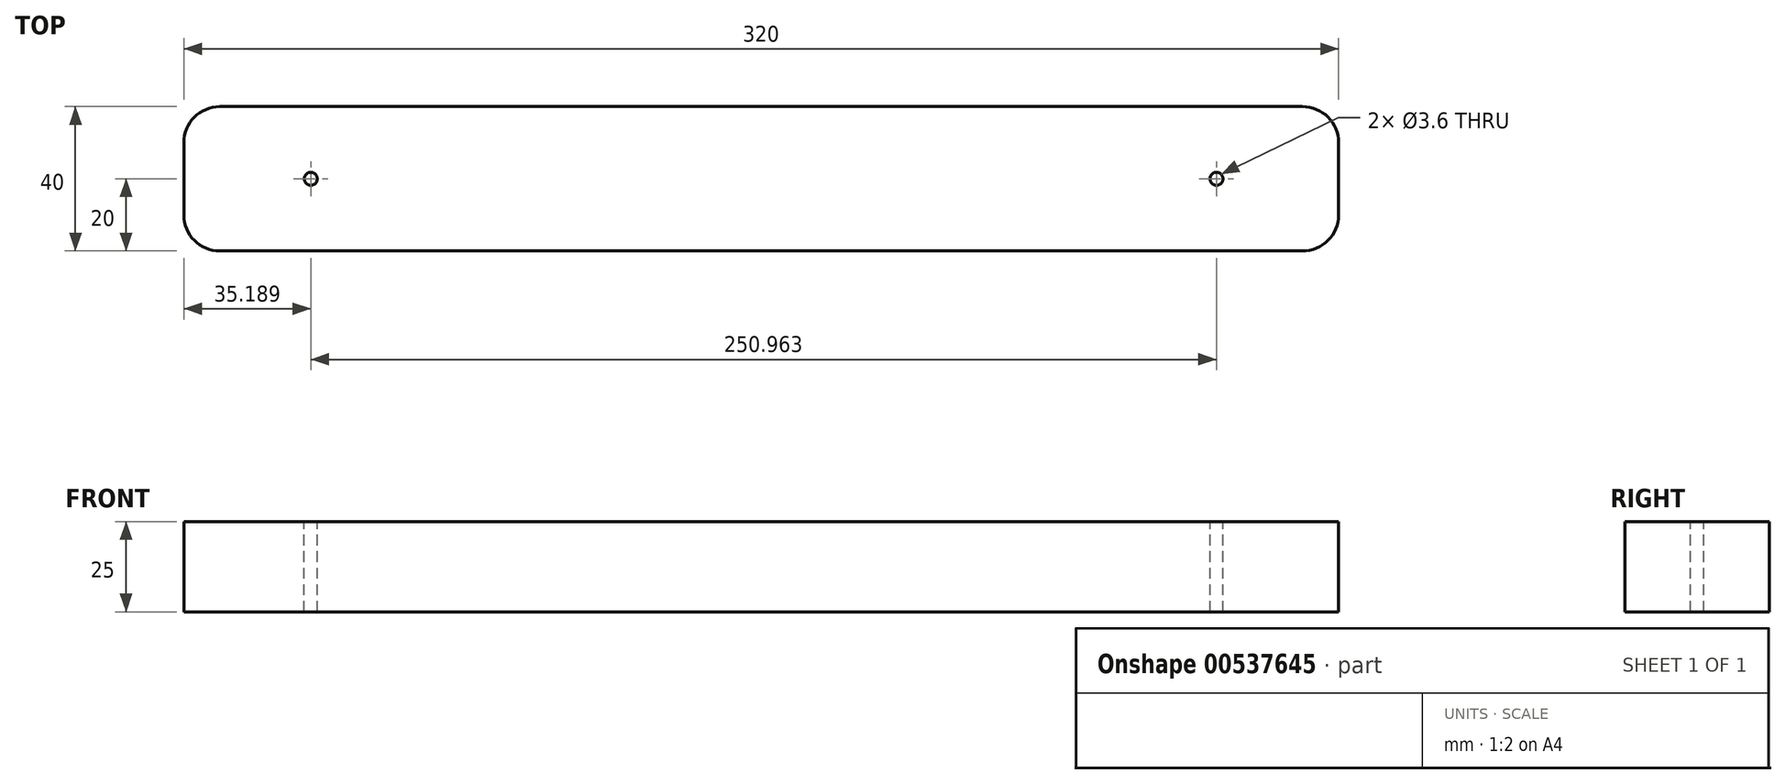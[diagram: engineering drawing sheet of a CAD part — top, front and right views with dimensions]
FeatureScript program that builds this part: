
annotation { "Feature Type Name" : "Feature", "Feature Type Description" : "" }
export const myFeature = defineFeature(function(context is Context, id is Id, definition is map)
    precondition{}
    {
        {
            var Q0;
            Q0=qCreatedBy(makeId("Top.planeOp"),FACE);
            var sketch = newSketch(context, id + "F0", { "sketchPlane" : qUnion([Q0])});
            skLineSegment(sketch, "E0.bottom", {"start": v(150, 20) * mm, "end": v(-150, 20) * mm});
            skLineSegment(sketch, "E0.top", {"start": v(150, -20) * mm, "end": v(-150, -20) * mm});
            skLineSegment(sketch, "E0.left", {"start": v(160, 10) * mm, "end": v(160, -10) * mm});
            skLineSegment(sketch, "E0.right", {"start": v(-160, 10) * mm, "end": v(-160, -10) * mm});
            skPoint(sketch, "E0.middle", {"position": v(0, 0) * mm});
            skPoint(sketch, "E1.visualSharp", {"position": v(-160, 20) * mm});
            skArc(sketch, "E1.filletArc", {"start": v(-150, 20) * mm, "mid": v(-157.07, 17.07) * mm, "end": v(-160, 10) * mm});
            skPoint(sketch, "E2.visualSharp", {"position": v(-160, -20) * mm});
            skArc(sketch, "E2.filletArc", {"start": v(-160, -10) * mm, "mid": v(-157.07, -17.07) * mm, "end": v(-150, -20) * mm});
            skPoint(sketch, "E3.visualSharp", {"position": v(160, 20) * mm});
            skArc(sketch, "E3.filletArc", {"start": v(160, 10) * mm, "mid": v(157.07, 17.07) * mm, "end": v(150, 20) * mm});
            skPoint(sketch, "E4.visualSharp", {"position": v(160, -20) * mm});
            skArc(sketch, "E4.filletArc", {"start": v(150, -20) * mm, "mid": v(157.07, -17.07) * mm, "end": v(160, -10) * mm});
            skSolve(sketch);
        }
        {
            var Q0;
            Q0 = qSketchRegion(id + "F0", true);
            extrude(context, id + "F1", {"entities" : qUnion([Q0]), "endBound" : BoundingType.SYMMETRIC, "depth" : 25 * mm, "offsetDistance" : 25 * mm});
        }
        {
            var Q0;
            Q0=makeQuery(id+"F1.opExtrude","CAP_FACE",FACE,{"disambiguationData":[OSD([sQuery(id+"F0.wireOp",EDGE,"E0.bottom"),sQuery(id+"F0.wireOp",EDGE,"E0.top"),sQuery(id+"F0.wireOp",EDGE,"E0.left"),sQuery(id+"F0.wireOp",EDGE,"E0.right"),sQuery(id+"F0.wireOp",EDGE,"E1.filletArc"),sQuery(id+"F0.wireOp",EDGE,"E2.filletArc"),sQuery(id+"F0.wireOp",EDGE,"E3.filletArc"),sQuery(id+"F0.wireOp",EDGE,"E4.filletArc")])],"isStart":false});
            var sketch = newSketch(context, id + "F2", { "sketchPlane" : qUnion([Q0])});
            skCircle(sketch, "E5", {"center": v(-124.81, 0) * mm, "radius": 1.8 * mm});
            skPoint(sketch, "E5.centerSnap0", {"position": v(-160, 0) * mm});
            skSolve(sketch);
        }
        {
            var Q0;
            Q0 = qSketchRegion(id + "F2", true);
            extrude(context, id + "F3", {"entities" : qUnion([Q0]), "operationType" : NewBodyOperationType.REMOVE, "oppositeDirection" : true, "depth" : 26 * mm, "offsetDistance" : 25 * mm});
        }
        {
            var Q0;
            Q0=makeQuery(id+"F1.opExtrude","CAP_FACE",FACE,{"disambiguationData":[OSD([sQuery(id+"F0.wireOp",EDGE,"E0.bottom"),sQuery(id+"F0.wireOp",EDGE,"E0.top"),sQuery(id+"F0.wireOp",EDGE,"E0.left"),sQuery(id+"F0.wireOp",EDGE,"E0.right"),sQuery(id+"F0.wireOp",EDGE,"E1.filletArc"),sQuery(id+"F0.wireOp",EDGE,"E2.filletArc"),sQuery(id+"F0.wireOp",EDGE,"E3.filletArc"),sQuery(id+"F0.wireOp",EDGE,"E4.filletArc")])],"isStart":false});
            var sketch = newSketch(context, id + "F4", { "sketchPlane" : qUnion([Q0])});
            skCircle(sketch, "E6", {"center": v(126.15, 0) * mm, "radius": 1.8 * mm});
            skPoint(sketch, "E6.centerSnap0", {"position": v(160, 0) * mm});
            skSolve(sketch);
        }
        {
            var Q0;
            Q0 = qSketchRegion(id + "F4", true);
            extrude(context, id + "F5", {"entities" : qUnion([Q0]), "operationType" : NewBodyOperationType.REMOVE, "oppositeDirection" : true, "depth" : 26 * mm, "offsetDistance" : 25 * mm});
        }
    });
